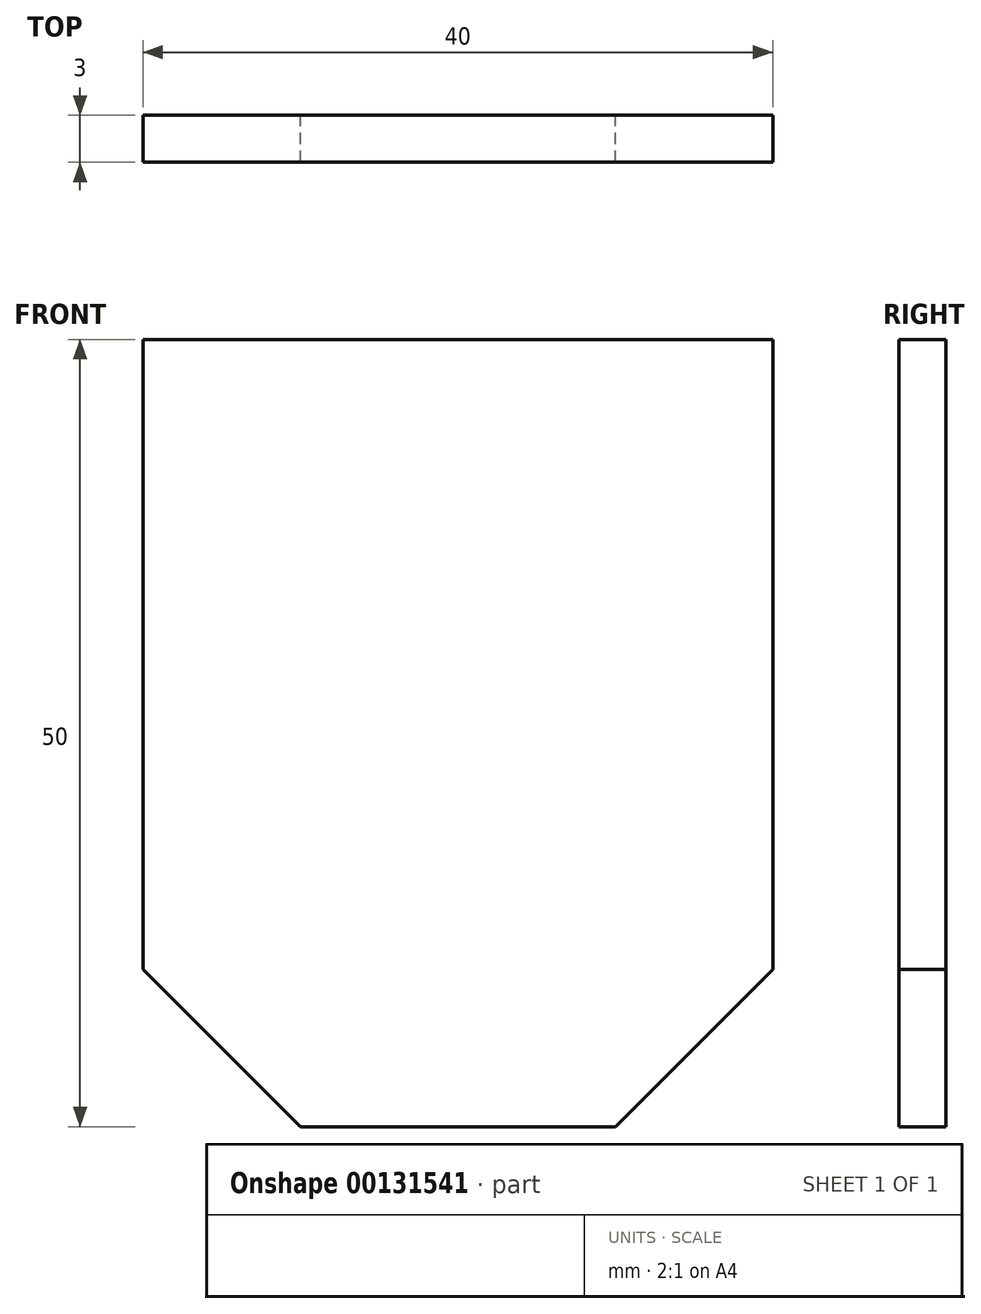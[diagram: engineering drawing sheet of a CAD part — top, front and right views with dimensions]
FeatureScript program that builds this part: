
annotation { "Feature Type Name" : "Feature", "Feature Type Description" : "" }
export const myFeature = defineFeature(function(context is Context, id is Id, definition is map)
    precondition{}
    {
        {
            var Q0;
            Q0=qCreatedBy(makeId("Front.planeOp"),FACE);
            var sketch = newSketch(context, id + "F0", { "sketchPlane" : qUnion([Q0])});
            skLineSegment(sketch, "E0", {"start": v(-35.57, 34.05) * mm, "end": v(4.43, 34.05) * mm});
            skLineSegment(sketch, "E1", {"start": v(4.43, 34.05) * mm, "end": v(4.43, -5.95) * mm});
            skLineSegment(sketch, "E2", {"start": v(4.43, -5.95) * mm, "end": v(-5.57, -15.95) * mm});
            skLineSegment(sketch, "E3", {"start": v(-5.57, -15.95) * mm, "end": v(-25.57, -15.95) * mm});
            skLineSegment(sketch, "E4", {"start": v(-25.57, -15.95) * mm, "end": v(-35.57, -5.95) * mm});
            skLineSegment(sketch, "E5", {"start": v(-35.57, -5.95) * mm, "end": v(-35.57, 34.05) * mm});
            skSolve(sketch);
        }
        {
            var Q0;
            Q0 = qSketchRegion(id + "F0", true);
            extrude(context, id + "F1", {"entities" : qUnion([Q0]), "depth" : 3 * mm});
        }
    });
